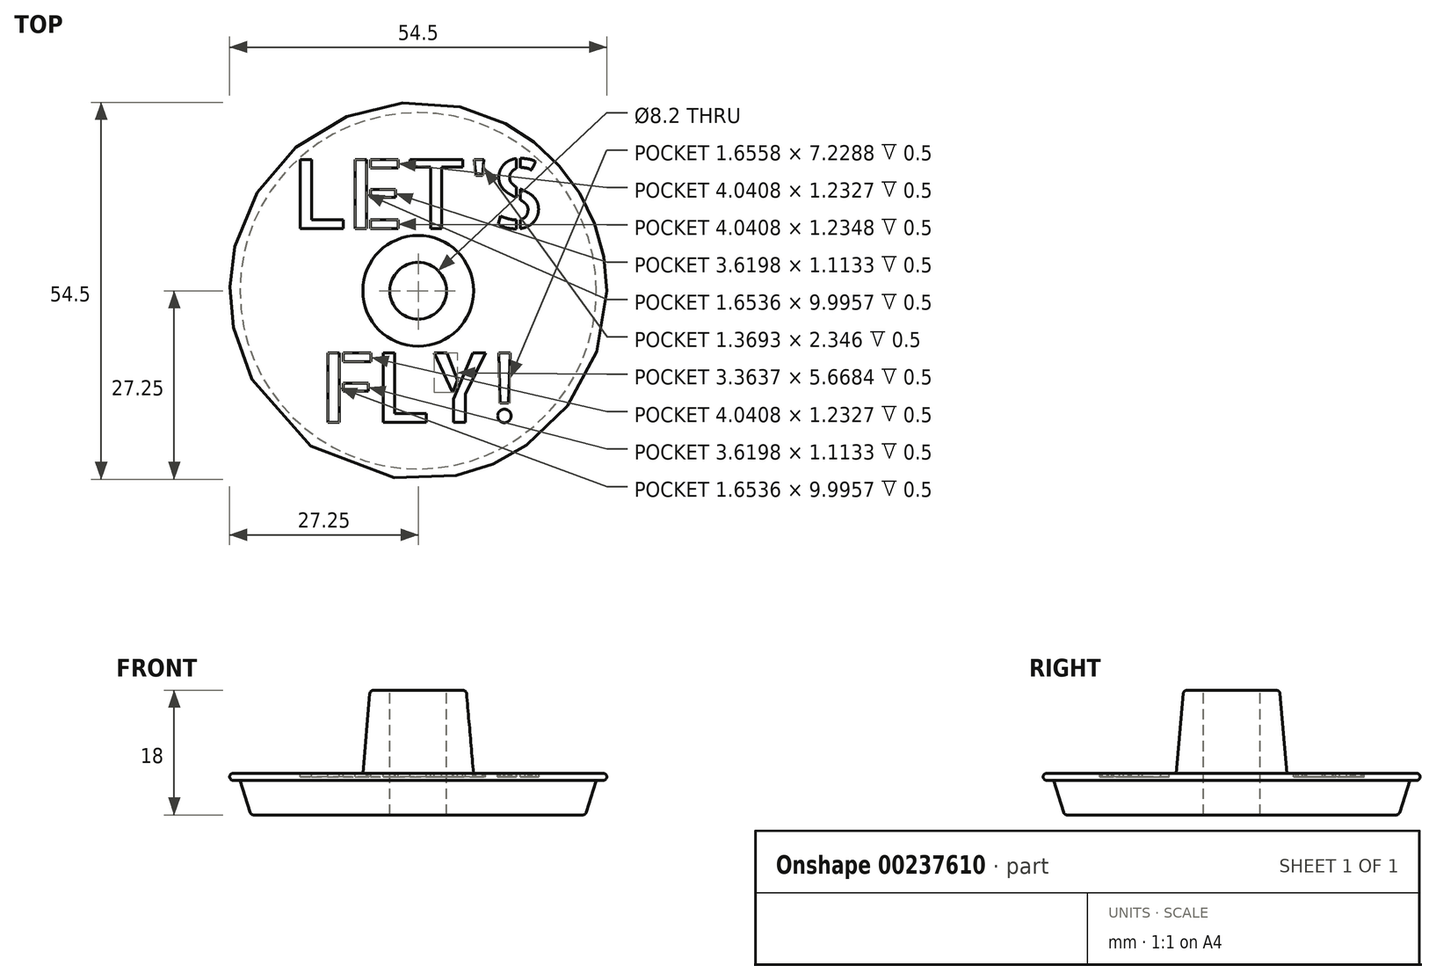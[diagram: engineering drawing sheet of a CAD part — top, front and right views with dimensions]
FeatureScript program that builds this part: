
annotation { "Feature Type Name" : "Feature", "Feature Type Description" : "" }
export const myFeature = defineFeature(function(context is Context, id is Id, definition is map)
    precondition{}
    {
        {
            var Q0;
            Q0=qCreatedBy(makeId("Top.planeOp"),FACE);
            var sketch = newSketch(context, id + "F0", { "sketchPlane" : qUnion([Q0])});
            skCircle(sketch, "E0", {"center": v(0, 0) * mm, "radius": 27.25 * mm});
            skCircle(sketch, "E1", {"center": v(0, 0) * mm, "radius": 25.75 * mm});
            skCircle(sketch, "E2", {"center": v(0, 0) * mm, "radius": 24.25 * mm});
            skSolve(sketch);
        }
        {
            var Q0;
            Q0 = qSketchRegion(id + "F0", true);
            var Q1;
            Q1=makeQuery(id+"F0.imprint","IMPRINT",FACE,{"disambiguationData":[TD([[makeQuery(id+"F0.imprint","IMPRINT",EDGE,{"derivedFrom":sQuery(id+"F0.wireOp",EDGE,"E1")}),1.0]])]});
            var Q2;
            Q2=makeQuery(id+"F0.imprint","IMPRINT",FACE,{"disambiguationData":[TD([[makeQuery(id+"F0.imprint","IMPRINT",EDGE,{"derivedFrom":sQuery(id+"F0.wireOp",EDGE,"E2")}),1.0]])]});
            extrude(context, id + "F1", {"entities" : qUnion([Q0, Q1, Q2]), "depth" : 1 * mm});
        }
        {
            var Q0;
            Q0=makeQuery(id+"F0.imprint","IMPRINT",FACE,{"disambiguationData":[TD([[makeQuery(id+"F0.imprint","IMPRINT",EDGE,{"derivedFrom":sQuery(id+"F0.wireOp",EDGE,"E1")}),1.0]])]});
            var Q1;
            Q1=makeQuery(id+"F0.imprint","IMPRINT",FACE,{"disambiguationData":[TD([[makeQuery(id+"F0.imprint","IMPRINT",EDGE,{"derivedFrom":sQuery(id+"F0.wireOp",EDGE,"E2")}),1.0]])]});
            extrude(context, id + "F2", {"entities" : qUnion([Q0, Q1]), "operationType" : NewBodyOperationType.ADD, "oppositeDirection" : true, "depth" : 5 * mm, "hasDraft" : true, "draftAngle" : 17.5 * degree, "draftPullDirection" : true});
        }
        {
            var Q0;
            Q0=makeQuery(id+"F1.opExtrude","CAP_FACE",FACE,{"disambiguationData":[OSD([sQuery(id+"F0.wireOp",EDGE,"E0")])],"isStart":false});
            var sketch = newSketch(context, id + "F3", { "sketchPlane" : qUnion([Q0])});
            skCircle(sketch, "E3", {"center": v(0, 0) * mm, "radius": 8 * mm});
            skSolve(sketch);
        }
        {
            var Q0;
            Q0=makeQuery(id+"F3.imprint","IMPRINT",FACE,{"disambiguationData":[TD([[makeQuery(id+"F3.imprint","IMPRINT",EDGE,{"derivedFrom":sQuery(id+"F3.wireOp",EDGE,"E3")}),1.0]])]});
            extrude(context, id + "F4", {"entities" : qUnion([Q0]), "operationType" : NewBodyOperationType.ADD, "depth" : 12 * mm, "hasDraft" : true, "draftAngle" : 5 * degree, "draftPullDirection" : true});
        }
        {
            var Q0;
            Q0=makeQuery(id+"F4.opExtrude","CAP_FACE",FACE,{"disambiguationData":[OSD([sQuery(id+"F3.wireOp",EDGE,"E3")])],"isStart":false});
            var sketch = newSketch(context, id + "F5", { "sketchPlane" : qUnion([Q0])});
            skCircle(sketch, "E4", {"center": v(0, 0) * mm, "radius": 4.1 * mm});
            skSolve(sketch);
        }
        {
            var Q0;
            Q0 = qSketchRegion(id + "F5", true);
            extrude(context, id + "F6", {"entities" : qUnion([Q0]), "operationType" : NewBodyOperationType.REMOVE, "endBound" : BoundingType.UP_TO_NEXT, "oppositeDirection" : true, "depth" : 25 * mm});
        }
        {
            var Q0;
            Q0=makeQuery(id+"F1.opExtrude","CAP_FACE",FACE,{"disambiguationData":[OSD([sQuery(id+"F0.wireOp",EDGE,"E0")])],"isStart":false});
            var sketch = newSketch(context, id + "F7", { "sketchPlane" : qUnion([Q0])});
            skText(sketch, "E5", { "text": "LET\'S", "fontName": "AllertaStencil-Regular.ttf"});
            skText(sketch, "E6", { "text": "FLY!", "fontName": "AllertaStencil-Regular.ttf"});
            skLineSegment(sketch, "E7", {"start": v(0, 8) * mm, "end": v(0, 27.25) * mm, "construction": true});
            skLineSegment(sketch, "E8", {"start": v(0, -8) * mm, "end": v(0, -27.25) * mm, "construction": true});
            skLineSegment(sketch, "E9", {"start": v(-27.25, 0) * mm, "end": v(27.25, 0) * mm, "construction": true});
            const initialGuessF7  = {"E5": [-0.01833, 0.009, 1, 0, 0.01], "E6": [-0.01435, -0.019, 1, 0, 0.01]};
            skSetInitialGuess(sketch, initialGuessF7);
            skSolve(sketch);
        }
        {
            var Q0;
            Q0 = qSketchRegion(id + "F7", true);
            extrude(context, id + "F8", {"entities" : qUnion([Q0]), "operationType" : NewBodyOperationType.REMOVE, "oppositeDirection" : true, "depth" : .5 * mm});
        }
        {
            var Q0;
            Q0=makeQuery(id+"F2.opExtrude","CAP_EDGE",EDGE,{"disambiguationData":[OSD([sQuery(id+"F0.wireOp",EDGE,"E1")])],"isStart":false});
            var Q1;
            Q1=makeQuery(id+"F1.opExtrude","CAP_EDGE",EDGE,{"disambiguationData":[OSD([sQuery(id+"F0.wireOp",EDGE,"E0")])],"isStart":true});
            var Q2;
            Q2=makeQuery(id+"F1.opExtrude","CAP_EDGE",EDGE,{"disambiguationData":[OSD([sQuery(id+"F0.wireOp",EDGE,"E0")])],"isStart":false});
            var Q3;
            Q3=makeQuery(id+"F6.boolean.opBoolean","COPY",EDGE,{"derivedFrom":makeQuery(id+"F6.opExtrude","CAP_EDGE",EDGE,{"disambiguationData":[OSD([sQuery(id+"F5.wireOp",EDGE,"E4")])],"isStart":false})});
            var Q4;
            Q4=makeQuery(id+"F4.opExtrude","CAP_EDGE",EDGE,{"disambiguationData":[OSD([sQuery(id+"F3.wireOp",EDGE,"E3")])],"isStart":true});
            var Q5;
            Q5=makeQuery(id+"F4.opExtrude","CAP_EDGE",EDGE,{"disambiguationData":[OSD([sQuery(id+"F3.wireOp",EDGE,"E3")])],"isStart":false});
            var Q6;
            Q6=makeQuery(id+"F6.boolean.opBoolean","COPY",EDGE,{"derivedFrom":makeQuery(id+"F6.opExtrude","CAP_EDGE",EDGE,{"disambiguationData":[OSD([sQuery(id+"F5.wireOp",EDGE,"E4")])],"isStart":true})});
            fillet(context, id + "F9", {"entities" : qUnion([Q0, Q1, Q2, Q3, Q4, Q5, Q6]), "radius" : .5 * mm, "tangentPropagation" : true, "allowEdgeOverflow" : false});
        }
    });
